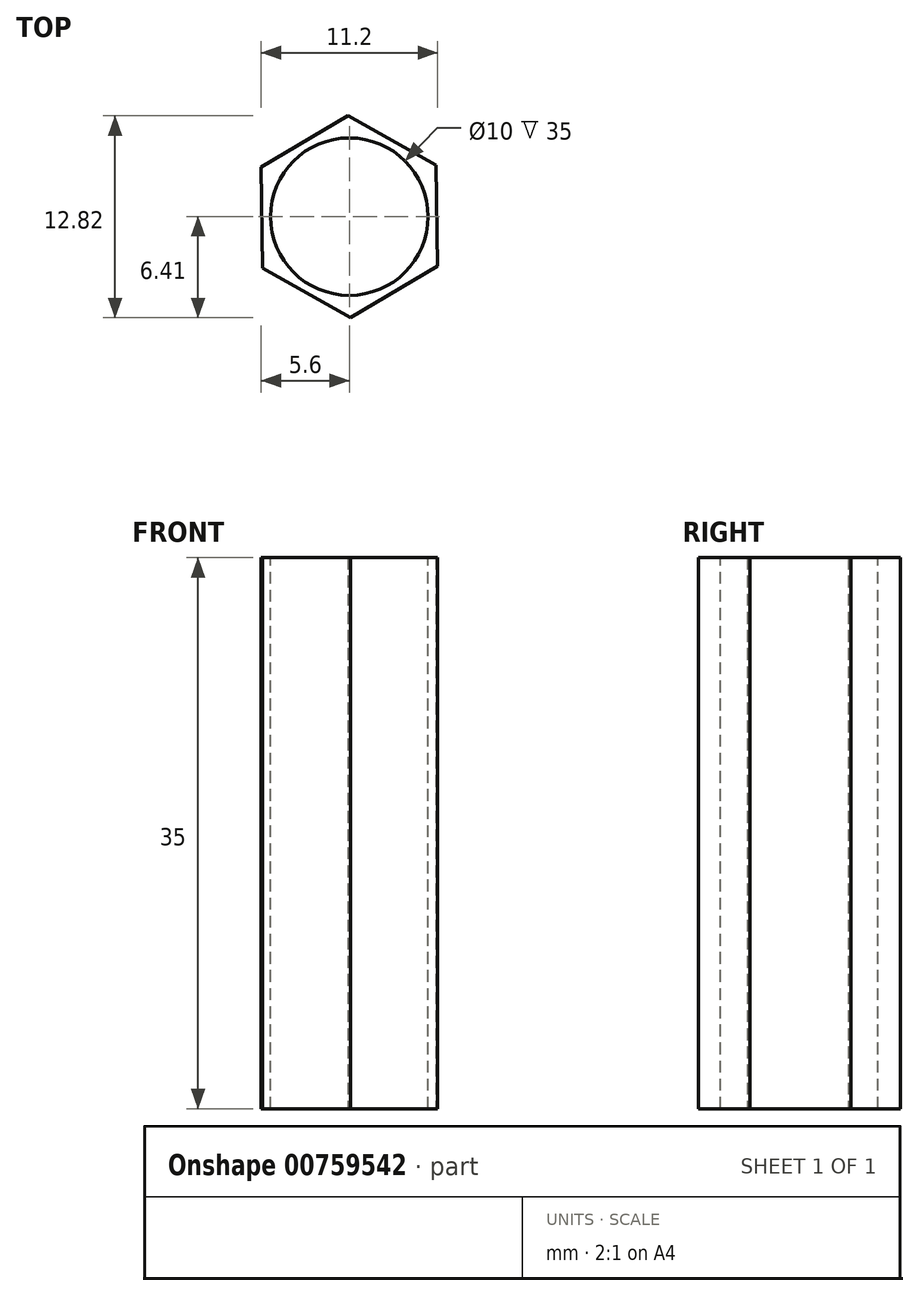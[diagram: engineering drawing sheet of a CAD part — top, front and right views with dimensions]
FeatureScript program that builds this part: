
annotation { "Feature Type Name" : "Feature", "Feature Type Description" : "" }
export const myFeature = defineFeature(function(context is Context, id is Id, definition is map)
    precondition{}
    {
        {
            var Q0;
            Q0=qCreatedBy(makeId("Top.planeOp"),FACE);
            var sketch = newSketch(context, id + "F0", { "sketchPlane" : qUnion([Q0])});
            skCircle(sketch, "E0.cCircle", {"center": v(0, 0) * mm, "radius": 5.55 * mm, "construction": true});
            skLineSegment(sketch, "E0.0", {"start": v(-0.08, 6.41) * mm, "end": v(5.51, 3.28) * mm});
            skLineSegment(sketch, "E0.1", {"start": v(5.51, 3.28) * mm, "end": v(5.6, -3.14) * mm});
            skLineSegment(sketch, "E0.2", {"start": v(5.6, -3.14) * mm, "end": v(0.08, -6.41) * mm});
            skLineSegment(sketch, "E0.3", {"start": v(0.08, -6.41) * mm, "end": v(-5.51, -3.28) * mm});
            skLineSegment(sketch, "E0.4", {"start": v(-5.51, -3.28) * mm, "end": v(-5.6, 3.14) * mm});
            skLineSegment(sketch, "E0.5", {"start": v(-5.6, 3.14) * mm, "end": v(-0.08, 6.41) * mm});
            skPoint(sketch, "E0.0.midPoint", {"position": v(2.72, 4.85) * mm});
            skSolve(sketch);
        }
        {
            var Q0;
            Q0 = qSketchRegion(id + "F0", true);
            extrude(context, id + "F1", {"entities" : qUnion([Q0]), "depth" : 35 * mm, "offsetDistance" : 25 * mm});
        }
        {
            var Q0;
            Q0=makeQuery(id+"F1.opExtrude","CAP_FACE",FACE,{"disambiguationData":[OSD([sQuery(id+"F0.wireOp",EDGE,"E0.0"),sQuery(id+"F0.wireOp",EDGE,"E0.1"),sQuery(id+"F0.wireOp",EDGE,"E0.2"),sQuery(id+"F0.wireOp",EDGE,"E0.3"),sQuery(id+"F0.wireOp",EDGE,"E0.4"),sQuery(id+"F0.wireOp",EDGE,"E0.5")])],"isStart":false});
            var sketch = newSketch(context, id + "F2", { "sketchPlane" : qUnion([Q0])});
            skCircle(sketch, "E1", {"center": v(0, 0) * mm, "radius": 5 * mm});
            skSolve(sketch);
        }
        {
            var Q0;
            Q0 = qSketchRegion(id + "F2", true);
            extrude(context, id + "F3", {"entities" : qUnion([Q0]), "operationType" : NewBodyOperationType.REMOVE, "oppositeDirection" : true, "depth" : 52.1 * mm, "offsetDistance" : 25 * mm});
        }
    });
